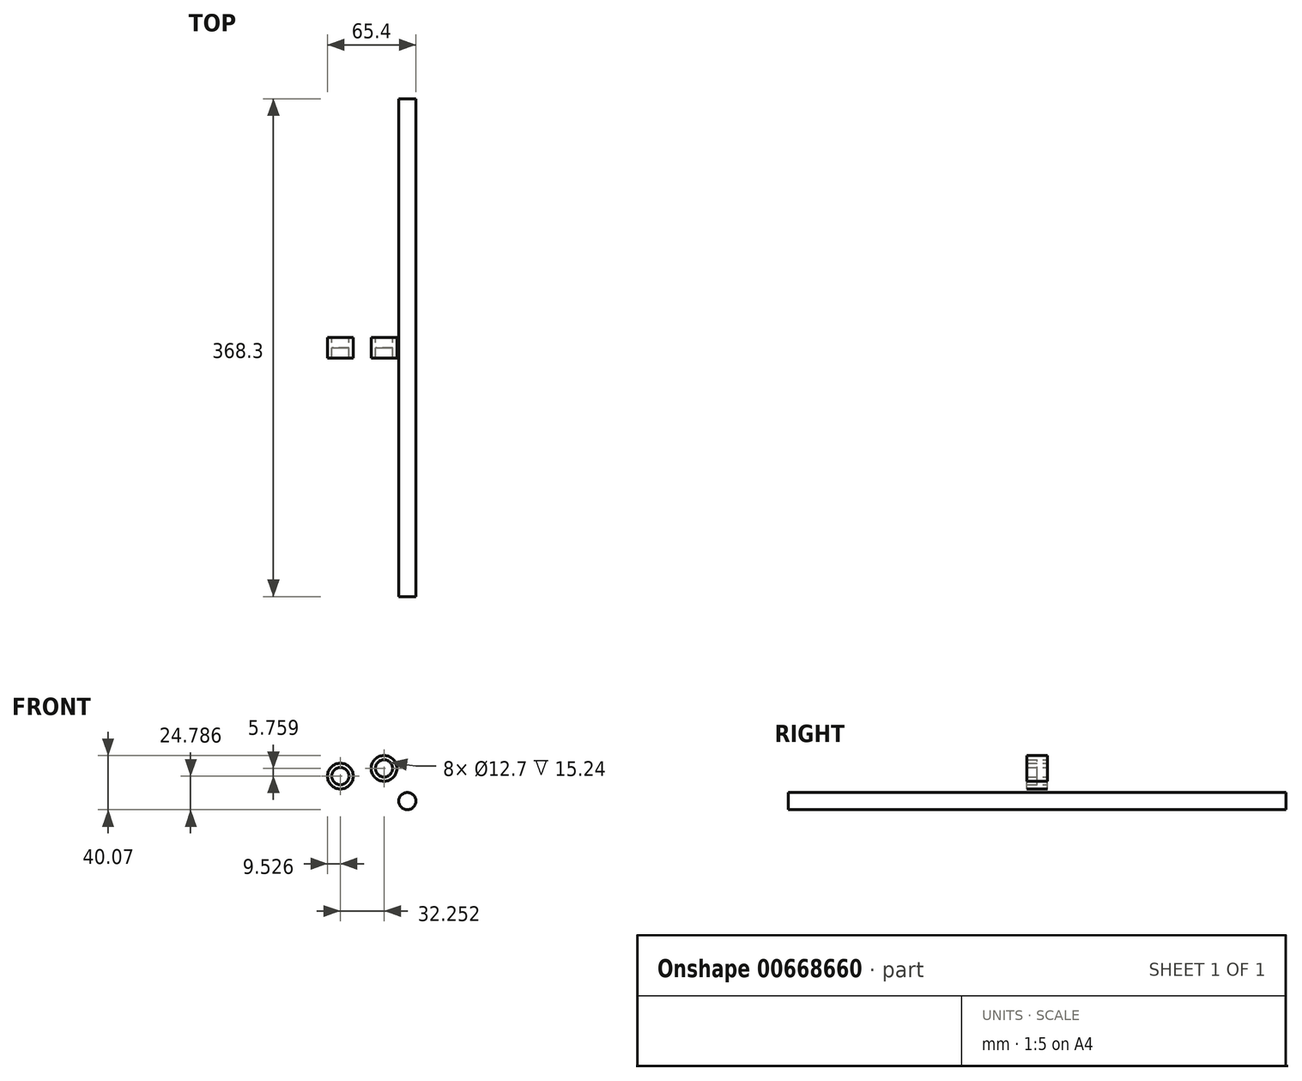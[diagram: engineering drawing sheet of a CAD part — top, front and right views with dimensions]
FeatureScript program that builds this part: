
annotation { "Feature Type Name" : "Feature", "Feature Type Description" : "" }
export const myFeature = defineFeature(function(context is Context, id is Id, definition is map)
    precondition{}
    {
        {
            var Q0;
            Q0=qCreatedBy(makeId("Front.planeOp"),FACE);
            var sketch = newSketch(context, id + "F0", { "sketchPlane" : qUnion([Q0])});
            skCircle(sketch, "E0", {"center": v(0, 0) * mm, "radius": 6.35 * mm});
            skCircle(sketch, "E1", {"center": v(-49.52, 18.44) * mm, "radius": 9.53 * mm});
            skCircle(sketch, "E2", {"center": v(-17.27, 24.2) * mm, "radius": 9.53 * mm});
            skCircle(sketch, "E3", {"center": v(-49.52, 18.44) * mm, "radius": 6.35 * mm});
            skCircle(sketch, "E4", {"center": v(-17.27, 24.2) * mm, "radius": 6.35 * mm});
            skLineSegment(sketch, "E5", {"start": v(-49.52, 24.79) * mm, "end": v(-49.52, 12.09) * mm});
            skLineSegment(sketch, "E6", {"start": v(-17.27, 30.54) * mm, "end": v(-17.27, 17.84) * mm});
            skSolve(sketch);
        }
        {
            var Q0;
            Q0=makeQuery(id+"F0.imprint","IMPRINT",FACE,{"disambiguationData":[TD([[makeQuery(id+"F0.imprint","IMPRINT",EDGE,{"derivedFrom":sQuery(id+"F0.wireOp",EDGE,"E0")}),1.0]])]});
            extrude(context, id + "F1", {"entities" : qUnion([Q0]), "endBound" : BoundingType.SYMMETRIC, "depth" : 368.3 * mm, "offsetDistance" : 25.4 * mm});
        }
        {
            var Q0;
            Q0=makeQuery(id+"F0.imprint","IMPRINT",FACE,{"disambiguationData":[TD([[makeQuery(id+"F0.imprint","IMPRINT",EDGE,{"derivedFrom":sQuery(id+"F0.wireOp",EDGE,"E1")}),1.0]])]});
            var Q1;
            Q1=makeQuery(id+"F0.imprint","IMPRINT",FACE,{"disambiguationData":[TD([[makeQuery(id+"F0.imprint","IMPRINT",EDGE,{"derivedFrom":sQuery(id+"F0.wireOp",EDGE,"E2")}),1.0]])]});
            extrude(context, id + "F2", {"entities" : qUnion([Q0, Q1]), "endBound" : BoundingType.SYMMETRIC, "depth" : 15.24 * mm, "offsetDistance" : 25.4 * mm});
        }
        {
            var Q0;
            Q0=makeQuery(id+"F0.imprint","IMPRINT",FACE,{"disambiguationData":[TD([[makeQuery(id+"F0.imprint","IMPRINT",EDGE,{"derivedFrom":sQuery(id+"F0.wireOp",EDGE,"E4")}),1.0]])]});
            var Q1;
            Q1=makeQuery(id+"F0.imprint","IMPRINT",FACE,{"disambiguationData":[TD([[makeQuery(id+"F0.imprint","IMPRINT",EDGE,{"derivedFrom":sQuery(id+"F0.wireOp",EDGE,"E3")}),1.0]])]});
            extrude(context, id + "F3", {"entities" : qUnion([Q0, Q1]), "depth" : 7.62 * mm, "offsetDistance" : 25.4 * mm});
        }
    });
